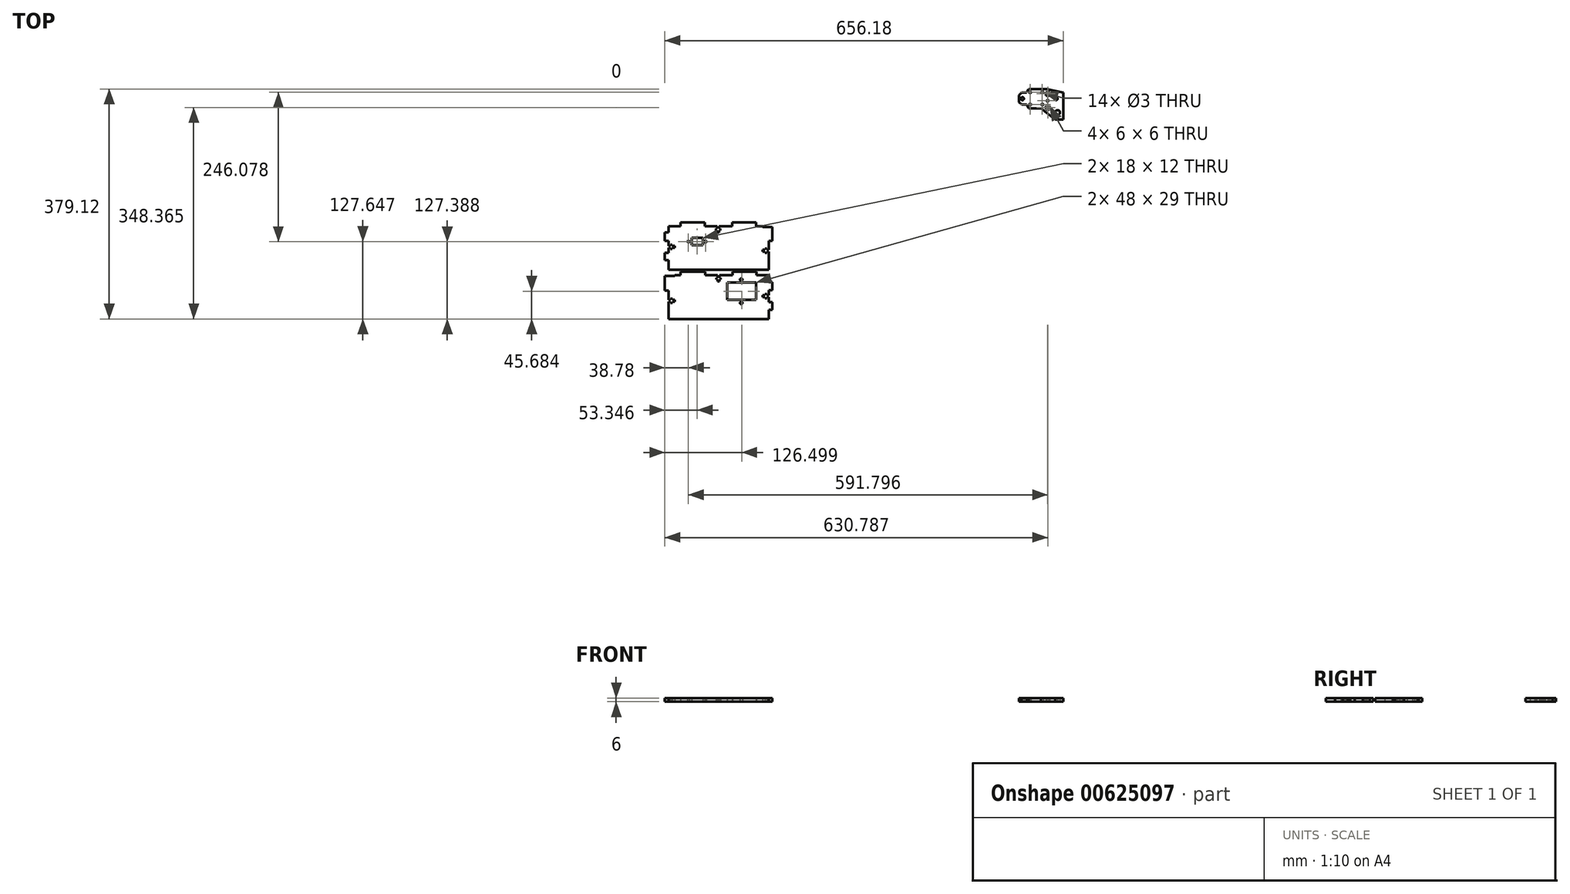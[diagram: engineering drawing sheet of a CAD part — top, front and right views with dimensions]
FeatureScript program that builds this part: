
annotation { "Feature Type Name" : "Feature", "Feature Type Description" : "" }
export const myFeature = defineFeature(function(context is Context, id is Id, definition is map)
    precondition{}
    {
        {
            var Q0;
            Q0=qCreatedBy(makeId("Top.planeOp"),FACE);
            var sketch = newSketch(context, id + "F0", { "sketchPlane" : qUnion([Q0])});
            skLineSegment(sketch, "E0", {"start": v(-400.96, 215.45) * mm, "end": v(-400.96, 196.55) * mm, "construction": true});
            skLineSegment(sketch, "E1", {"start": v(399.04, 218.3) * mm, "end": v(399.04, 197.18) * mm, "construction": true});
            skLineSegment(sketch, "E2", {"start": v(-18.25, 53.91) * mm, "end": v(81.75, 53.91) * mm});
            skLineSegment(sketch, "E3", {"start": v(81.75, 53.91) * mm, "end": v(81.75, 33.91) * mm});
            skLineSegment(sketch, "E4", {"start": v(81.75, 33.91) * mm, "end": v(41.75, -46.09) * mm});
            skLineSegment(sketch, "E5", {"start": v(41.75, -46.09) * mm, "end": v(21.75, -46.09) * mm});
            skLineSegment(sketch, "E6", {"start": v(21.75, -46.09) * mm, "end": v(-18.25, 33.91) * mm});
            skLineSegment(sketch, "E7", {"start": v(-18.25, 33.91) * mm, "end": v(-18.25, 53.91) * mm});
            skLineSegment(sketch, "E8", {"start": v(31.75, 53.91) * mm, "end": v(31.75, -82.9) * mm, "construction": true});
            skPoint(sketch, "E9", {"position": v(-362.77, -178.41) * mm});
            skPoint(sketch, "E10", {"position": v(-388.62, -185.6) * mm});
            skLineSegment(sketch, "E11.bottom", {"start": v(-388.62, -178.41) * mm, "end": v(-211.62, -178.41) * mm});
            skLineSegment(sketch, "E11.top", {"start": v(-388.62, -256.41) * mm, "end": v(-211.62, -256.41) * mm});
            skLineSegment(sketch, "E11.left", {"start": v(-388.62, -178.41) * mm, "end": v(-388.62, -256.41) * mm});
            skLineSegment(sketch, "E11.right", {"start": v(-211.62, -178.41) * mm, "end": v(-211.62, -256.41) * mm});
            skLineSegment(sketch, "E12", {"start": v(-388.62, -209.41) * mm, "end": v(-382.62, -209.41) * mm});
            skLineSegment(sketch, "E13", {"start": v(-382.62, -209.41) * mm, "end": v(-382.62, -256.41) * mm});
            skLineSegment(sketch, "E14", {"start": v(-322.26, -178.41) * mm, "end": v(-322.26, -184.41) * mm});
            skLineSegment(sketch, "E15", {"start": v(-322.26, -184.41) * mm, "end": v(-277.26, -184.41) * mm});
            skLineSegment(sketch, "E16", {"start": v(-277.26, -184.41) * mm, "end": v(-277.26, -178.41) * mm});
            skLineSegment(sketch, "E17", {"start": v(-388.62, -185.6) * mm, "end": v(-372.39, -185.6) * mm});
            skLineSegment(sketch, "E18", {"start": v(-372.39, -185.6) * mm, "end": v(-372.39, -184.41) * mm});
            skLineSegment(sketch, "E19", {"start": v(-372.39, -184.41) * mm, "end": v(-362.77, -184.41) * mm});
            skLineSegment(sketch, "E20", {"start": v(-362.77, -184.41) * mm, "end": v(-362.77, -178.41) * mm});
            skLineSegment(sketch, "E21", {"start": v(-237.45, -178.41) * mm, "end": v(-237.45, -184.41) * mm});
            skLineSegment(sketch, "E22", {"start": v(-237.45, -184.41) * mm, "end": v(-217.62, -184.41) * mm});
            skLineSegment(sketch, "E23", {"start": v(-217.62, -184.41) * mm, "end": v(-217.62, -195.47) * mm});
            skLineSegment(sketch, "E24", {"start": v(-217.62, -195.47) * mm, "end": v(-211.62, -195.47) * mm});
            skLineSegment(sketch, "E25", {"start": v(-211.62, -208.93) * mm, "end": v(-217.62, -208.93) * mm});
            skLineSegment(sketch, "E26", {"start": v(-217.62, -208.93) * mm, "end": v(-217.62, -228.93) * mm});
            skLineSegment(sketch, "E27", {"start": v(-217.62, -228.93) * mm, "end": v(-211.62, -228.93) * mm});
            skLineSegment(sketch, "E28", {"start": v(-211.62, -241.41) * mm, "end": v(-217.62, -241.41) * mm});
            skLineSegment(sketch, "E29", {"start": v(-217.62, -241.41) * mm, "end": v(-217.62, -256.41) * mm});
            skLineSegment(sketch, "E30.bottom", {"start": v(-286.12, -196.23) * mm, "end": v(-238.12, -196.23) * mm});
            skLineSegment(sketch, "E30.top", {"start": v(-286.12, -225.23) * mm, "end": v(-238.12, -225.23) * mm});
            skLineSegment(sketch, "E30.left", {"start": v(-286.12, -196.23) * mm, "end": v(-286.12, -225.23) * mm});
            skLineSegment(sketch, "E30.right", {"start": v(-238.12, -196.23) * mm, "end": v(-238.12, -225.23) * mm});
            skLineSegment(sketch, "E31", {"start": v(-382.62, -224.82) * mm, "end": v(-372.62, -224.82) * mm});
            skLineSegment(sketch, "E32", {"start": v(-372.62, -224.82) * mm, "end": v(-372.62, -227.82) * mm});
            skLineSegment(sketch, "E33", {"start": v(-372.62, -227.82) * mm, "end": v(-382.62, -227.82) * mm});
            skLineSegment(sketch, "E34", {"start": v(-379.34, -224.82) * mm, "end": v(-379.34, -222.82) * mm});
            skLineSegment(sketch, "E35", {"start": v(-379.34, -222.82) * mm, "end": v(-376.34, -222.82) * mm});
            skLineSegment(sketch, "E36", {"start": v(-376.34, -222.82) * mm, "end": v(-376.34, -224.82) * mm});
            skLineSegment(sketch, "E37", {"start": v(-379.27, -227.82) * mm, "end": v(-379.27, -229.82) * mm});
            skLineSegment(sketch, "E38", {"start": v(-379.27, -229.82) * mm, "end": v(-376.27, -229.82) * mm});
            skLineSegment(sketch, "E39", {"start": v(-376.27, -229.82) * mm, "end": v(-376.27, -227.82) * mm});
            skLineSegment(sketch, "E40", {"start": v(-301.63, -184.41) * mm, "end": v(-301.63, -194.41) * mm});
            skLineSegment(sketch, "E41", {"start": v(-301.63, -194.41) * mm, "end": v(-298.63, -194.41) * mm});
            skLineSegment(sketch, "E42", {"start": v(-298.63, -194.41) * mm, "end": v(-298.63, -184.41) * mm});
            skLineSegment(sketch, "E43", {"start": v(-303.63, -188.41) * mm, "end": v(-301.63, -188.41) * mm});
            skLineSegment(sketch, "E44", {"start": v(-296.63, -188.41) * mm, "end": v(-296.63, -191.41) * mm});
            skLineSegment(sketch, "E45", {"start": v(-296.63, -191.41) * mm, "end": v(-298.63, -191.41) * mm});
            skLineSegment(sketch, "E46.trimOffspring", {"start": v(-298.63, -188.41) * mm, "end": v(-296.63, -188.41) * mm});
            skLineSegment(sketch, "E47.trimOffspring", {"start": v(-301.63, -191.41) * mm, "end": v(-303.63, -191.41) * mm});
            skLineSegment(sketch, "E48", {"start": v(-303.63, -188.41) * mm, "end": v(-303.63, -191.41) * mm});
            skLineSegment(sketch, "E49", {"start": v(-217.62, -217.26) * mm, "end": v(-227.62, -217.26) * mm});
            skLineSegment(sketch, "E50", {"start": v(-227.62, -217.26) * mm, "end": v(-227.62, -220.26) * mm});
            skLineSegment(sketch, "E51", {"start": v(-227.62, -220.26) * mm, "end": v(-217.62, -220.26) * mm});
            skLineSegment(sketch, "E52.bottom", {"start": v(-223.46, -215.26) * mm, "end": v(-220.46, -215.26) * mm});
            skLineSegment(sketch, "E52.top", {"start": v(-223.46, -222.26) * mm, "end": v(-220.46, -222.26) * mm});
            skLineSegment(sketch, "E52.left", {"start": v(-223.46, -215.26) * mm, "end": v(-223.46, -222.26) * mm});
            skLineSegment(sketch, "E52.right", {"start": v(-220.46, -215.26) * mm, "end": v(-220.46, -222.26) * mm});
            skCircle(sketch, "E53", {"center": v(-262.81, -191.54) * mm, "radius": 2 * mm});
            skCircle(sketch, "E54", {"center": v(-262.81, -230.07) * mm, "radius": 2 * mm});
            skPoint(sketch, "E55", {"position": v(-362.84, -97.6) * mm});
            skLineSegment(sketch, "E56.bottom", {"start": v(-388.62, -97.6) * mm, "end": v(-211.62, -97.6) * mm});
            skLineSegment(sketch, "E56.top", {"start": v(-388.62, -175.6) * mm, "end": v(-211.62, -175.6) * mm});
            skLineSegment(sketch, "E56.left", {"start": v(-388.62, -97.6) * mm, "end": v(-388.62, -175.6) * mm});
            skLineSegment(sketch, "E56.right", {"start": v(-211.62, -97.6) * mm, "end": v(-211.62, -175.6) * mm});
            skLineSegment(sketch, "E57", {"start": v(-388.62, -113.85) * mm, "end": v(-382.62, -113.85) * mm});
            skLineSegment(sketch, "E58", {"start": v(-382.62, -113.85) * mm, "end": v(-382.62, -103.59) * mm});
            skLineSegment(sketch, "E59", {"start": v(-382.62, -103.59) * mm, "end": v(-362.62, -103.59) * mm});
            skLineSegment(sketch, "E60", {"start": v(-362.62, -103.59) * mm, "end": v(-362.84, -97.6) * mm});
            skLineSegment(sketch, "E61", {"start": v(-322.93, -97.6) * mm, "end": v(-322.93, -103.6) * mm});
            skLineSegment(sketch, "E62", {"start": v(-322.93, -103.6) * mm, "end": v(-277.93, -103.6) * mm});
            skLineSegment(sketch, "E63", {"start": v(-277.93, -103.6) * mm, "end": v(-277.93, -97.6) * mm});
            skLineSegment(sketch, "E64", {"start": v(-388.62, -127.72) * mm, "end": v(-382.62, -127.72) * mm});
            skLineSegment(sketch, "E65", {"start": v(-382.62, -127.72) * mm, "end": v(-382.62, -147.72) * mm});
            skLineSegment(sketch, "E66", {"start": v(-382.62, -147.72) * mm, "end": v(-390.27, -147.72) * mm});
            skLineSegment(sketch, "E67", {"start": v(-388.62, -159.6) * mm, "end": v(-382.62, -159.6) * mm});
            skLineSegment(sketch, "E68", {"start": v(-382.62, -159.6) * mm, "end": v(-382.62, -175.6) * mm});
            skLineSegment(sketch, "E69.bottom", {"start": v(-344.27, -122.76) * mm, "end": v(-326.27, -122.76) * mm});
            skLineSegment(sketch, "E69.top", {"start": v(-344.27, -134.76) * mm, "end": v(-326.27, -134.76) * mm});
            skLineSegment(sketch, "E69.left", {"start": v(-344.27, -122.76) * mm, "end": v(-344.27, -134.76) * mm});
            skLineSegment(sketch, "E69.right", {"start": v(-326.27, -122.76) * mm, "end": v(-326.27, -134.76) * mm});
            skCircle(sketch, "E70", {"center": v(-321.57, -129.02) * mm, "radius": 1.5 * mm});
            skCircle(sketch, "E71", {"center": v(-349.84, -129.02) * mm, "radius": 1.5 * mm});
            skLineSegment(sketch, "E72", {"start": v(-211.62, -127.6) * mm, "end": v(-217.62, -127.6) * mm});
            skLineSegment(sketch, "E73", {"start": v(-217.62, -127.6) * mm, "end": v(-217.62, -175.6) * mm});
            skLineSegment(sketch, "E74", {"start": v(-238.62, -97.6) * mm, "end": v(-238.62, -103.6) * mm});
            skLineSegment(sketch, "E75", {"start": v(-238.62, -103.6) * mm, "end": v(-227.62, -103.6) * mm});
            skLineSegment(sketch, "E76", {"start": v(-227.62, -103.6) * mm, "end": v(-227.62, -104.6) * mm});
            skLineSegment(sketch, "E77", {"start": v(-227.62, -104.6) * mm, "end": v(-211.62, -104.6) * mm});
            skLineSegment(sketch, "E78.bottom", {"start": v(-382.62, -135.99) * mm, "end": v(-372.62, -135.99) * mm});
            skLineSegment(sketch, "E78.top", {"start": v(-382.62, -138.99) * mm, "end": v(-372.62, -138.99) * mm});
            skLineSegment(sketch, "E78.left", {"start": v(-382.62, -135.99) * mm, "end": v(-382.62, -138.99) * mm});
            skLineSegment(sketch, "E78.right", {"start": v(-372.62, -135.99) * mm, "end": v(-372.62, -138.99) * mm});
            skLineSegment(sketch, "E79.bottom", {"start": v(-302.3, -103.6) * mm, "end": v(-299.3, -103.6) * mm});
            skLineSegment(sketch, "E79.top", {"start": v(-302.3, -113.6) * mm, "end": v(-299.3, -113.6) * mm});
            skLineSegment(sketch, "E79.left", {"start": v(-302.3, -103.6) * mm, "end": v(-302.3, -113.6) * mm});
            skLineSegment(sketch, "E79.right", {"start": v(-299.3, -103.6) * mm, "end": v(-299.3, -113.6) * mm});
            skLineSegment(sketch, "E80.bottom", {"start": v(-217.62, -142.67) * mm, "end": v(-227.62, -142.67) * mm});
            skLineSegment(sketch, "E80.top", {"start": v(-217.62, -145.67) * mm, "end": v(-227.62, -145.67) * mm});
            skLineSegment(sketch, "E80.left", {"start": v(-217.62, -142.67) * mm, "end": v(-217.62, -145.67) * mm});
            skLineSegment(sketch, "E80.right", {"start": v(-227.62, -142.67) * mm, "end": v(-227.62, -145.67) * mm});
            skLineSegment(sketch, "E81.bottom", {"start": v(-223.76, -140.67) * mm, "end": v(-220.76, -140.67) * mm});
            skLineSegment(sketch, "E81.top", {"start": v(-223.76, -147.67) * mm, "end": v(-220.76, -147.67) * mm});
            skLineSegment(sketch, "E81.left", {"start": v(-223.76, -140.67) * mm, "end": v(-223.76, -147.67) * mm});
            skLineSegment(sketch, "E81.right", {"start": v(-220.76, -140.67) * mm, "end": v(-220.76, -147.67) * mm});
            skLineSegment(sketch, "E82.bottom", {"start": v(-304.3, -107.4) * mm, "end": v(-297.3, -107.4) * mm});
            skLineSegment(sketch, "E82.top", {"start": v(-304.3, -110.4) * mm, "end": v(-297.3, -110.4) * mm});
            skLineSegment(sketch, "E82.left", {"start": v(-304.3, -107.4) * mm, "end": v(-304.3, -110.4) * mm});
            skLineSegment(sketch, "E82.right", {"start": v(-297.3, -107.4) * mm, "end": v(-297.3, -110.4) * mm});
            skLineSegment(sketch, "E83.bottom", {"start": v(-379.61, -133.99) * mm, "end": v(-376.61, -133.99) * mm});
            skLineSegment(sketch, "E83.top", {"start": v(-379.61, -140.99) * mm, "end": v(-376.61, -140.99) * mm});
            skLineSegment(sketch, "E83.left", {"start": v(-379.61, -133.99) * mm, "end": v(-379.61, -140.99) * mm});
            skLineSegment(sketch, "E83.right", {"start": v(-376.61, -133.99) * mm, "end": v(-376.61, -140.99) * mm});
            skLineSegment(sketch, "E84", {"start": v(210.6, 122.7) * mm, "end": v(240.6, 122.7) * mm});
            skLineSegment(sketch, "E85", {"start": v(240.6, 122.7) * mm, "end": v(267.56, 116.54) * mm});
            skLineSegment(sketch, "E86", {"start": v(267.56, 116.54) * mm, "end": v(267.56, 72.54) * mm});
            skLineSegment(sketch, "E87", {"start": v(267.56, 72.54) * mm, "end": v(254.56, 72.54) * mm});
            skLineSegment(sketch, "E88", {"start": v(254.56, 72.54) * mm, "end": v(230.6, 90.7) * mm});
            skLineSegment(sketch, "E89", {"start": v(230.6, 90.7) * mm, "end": v(210.6, 90.7) * mm});
            skLineSegment(sketch, "E90", {"start": v(210.6, 90.7) * mm, "end": v(207.37, 96.71) * mm});
            skLineSegment(sketch, "E91", {"start": v(207.37, 96.71) * mm, "end": v(199.07, 96.71) * mm});
            skLineSegment(sketch, "E92", {"start": v(199.07, 96.71) * mm, "end": v(194.7, 101.07) * mm});
            skLineSegment(sketch, "E93", {"start": v(194.7, 101.07) * mm, "end": v(194.7, 112.35) * mm});
            skLineSegment(sketch, "E94", {"start": v(194.7, 112.35) * mm, "end": v(199.07, 116.71) * mm});
            skLineSegment(sketch, "E95", {"start": v(199.07, 116.71) * mm, "end": v(207.37, 116.71) * mm});
            skLineSegment(sketch, "E96", {"start": v(207.37, 116.71) * mm, "end": v(210.6, 122.7) * mm});
            skLineSegment(sketch, "E97.bottom", {"start": v(239.2, 117.5) * mm, "end": v(245.2, 117.5) * mm});
            skLineSegment(sketch, "E97.top", {"start": v(239.2, 111.5) * mm, "end": v(245.2, 111.5) * mm});
            skLineSegment(sketch, "E97.left", {"start": v(239.2, 117.5) * mm, "end": v(239.2, 111.5) * mm});
            skLineSegment(sketch, "E97.right", {"start": v(245.2, 117.5) * mm, "end": v(245.2, 111.5) * mm});
            skLineSegment(sketch, "E98.bottom", {"start": v(239.17, 94.96) * mm, "end": v(245.17, 94.96) * mm});
            skLineSegment(sketch, "E98.top", {"start": v(239.17, 88.96) * mm, "end": v(245.17, 88.96) * mm});
            skLineSegment(sketch, "E98.left", {"start": v(239.17, 94.96) * mm, "end": v(239.17, 88.96) * mm});
            skLineSegment(sketch, "E98.right", {"start": v(245.17, 94.96) * mm, "end": v(245.17, 88.96) * mm});
            skCircle(sketch, "E99", {"center": v(200.33, 106.71) * mm, "radius": 2.5 * mm});
            skCircle(sketch, "E100", {"center": v(213.14, 117.06) * mm, "radius": 1.5 * mm});
            skCircle(sketch, "E101", {"center": v(213.14, 97.06) * mm, "radius": 1.5 * mm});
            skCircle(sketch, "E102", {"center": v(233.14, 97.06) * mm, "radius": 1.5 * mm});
            skCircle(sketch, "E103", {"center": v(233.14, 117.06) * mm, "radius": 1.5 * mm});
            skCircle(sketch, "E104", {"center": v(241.96, 103.18) * mm, "radius": 1.5 * mm});
            skCircle(sketch, "E105", {"center": v(255.73, 106.71) * mm, "radius": 2.5 * mm});
            skCircle(sketch, "E106", {"center": v(258.28, 83.74) * mm, "radius": 4 * mm});
            skLineSegment(sketch, "E107", {"start": v(192.03, 106.71) * mm, "end": v(273.18, 106.71) * mm, "construction": true});
            skSolve(sketch);
        }
        {
            var Q0;
            {var subQ25=sQuery(id+"F0.wireOp",EDGE,"E12");Q0=makeQuery(id+"F0.imprint","IMPRINT",FACE,{"disambiguationData":[TD([[makeQuery(id+"F0.imprint","IMPRINT",EDGE,{"derivedFrom":subQ25}),1.0]])]});}
            extrude(context, id + "F1", {"entities" : qUnion([Q0]), "depth" : 6 * mm, "offsetDistance" : 25 * mm});
        }
        {
            var Q0;
            {var subQ31=sQuery(id+"F0.wireOp",EDGE,"E57");Q0=makeQuery(id+"F0.imprint","IMPRINT",FACE,{"disambiguationData":[TD([[makeQuery(id+"F0.imprint","IMPRINT",EDGE,{"derivedFrom":subQ31}),-1.0]])]});}
            extrude(context, id + "F2", {"entities" : qUnion([Q0]), "depth" : 6 * mm, "offsetDistance" : 25 * mm});
        }
        {
            var Q0;
            Q0=makeQuery(id+"F0.imprint","IMPRINT",FACE,{"disambiguationData":[TD([[makeQuery(id+"F0.imprint","IMPRINT",EDGE,{"derivedFrom":sQuery(id+"F0.wireOp",EDGE,"E84")}),-1.0]])]});
            extrude(context, id + "F3", {"entities" : qUnion([Q0]), "depth" : 6 * mm, "offsetDistance" : 25 * mm});
        }
        {
            var Q0;
            Q0=sQuery(id+"F0.wireOp",VERTEX,"E100.center");
            var Q1;
            Q1=sQuery(id+"F0.wireOp",VERTEX,"E103.center");
            var Q2;
            Q2=sQuery(id+"F0.wireOp",VERTEX,"E101.center");
            var Q3;
            Q3=sQuery(id+"F0.wireOp",VERTEX,"E102.center");
            var Q4;
            Q4=sQuery(id+"F0.wireOp",VERTEX,"E104.center");
            var Q5;
            Q5=makeQuery(id+"F3.opExtrude","SWEPT_BODY",BODY,{"disambiguationData":[OSD([sQuery(id+"F0.wireOp",EDGE,"E84"),sQuery(id+"F0.wireOp",EDGE,"E85"),sQuery(id+"F0.wireOp",EDGE,"E86"),sQuery(id+"F0.wireOp",EDGE,"E87"),sQuery(id+"F0.wireOp",EDGE,"E88"),sQuery(id+"F0.wireOp",EDGE,"E89"),sQuery(id+"F0.wireOp",EDGE,"E90"),sQuery(id+"F0.wireOp",EDGE,"E91"),sQuery(id+"F0.wireOp",EDGE,"E92"),sQuery(id+"F0.wireOp",EDGE,"E93"),sQuery(id+"F0.wireOp",EDGE,"E94"),sQuery(id+"F0.wireOp",EDGE,"E95"),sQuery(id+"F0.wireOp",EDGE,"E96"),sQuery(id+"F0.wireOp",EDGE,"E97.bottom"),sQuery(id+"F0.wireOp",EDGE,"E97.top"),sQuery(id+"F0.wireOp",EDGE,"E97.left"),sQuery(id+"F0.wireOp",EDGE,"E97.right"),sQuery(id+"F0.wireOp",EDGE,"E98.bottom"),sQuery(id+"F0.wireOp",EDGE,"E98.top"),sQuery(id+"F0.wireOp",EDGE,"E98.left"),sQuery(id+"F0.wireOp",EDGE,"E98.right"),sQuery(id+"F0.wireOp",EDGE,"E99"),sQuery(id+"F0.wireOp",EDGE,"E100"),sQuery(id+"F0.wireOp",EDGE,"E101"),sQuery(id+"F0.wireOp",EDGE,"E102"),sQuery(id+"F0.wireOp",EDGE,"E103"),sQuery(id+"F0.wireOp",EDGE,"E104"),sQuery(id+"F0.wireOp",EDGE,"E105"),sQuery(id+"F0.wireOp",EDGE,"E106")])]});
            hole(context, id + "F4", {"style" : HoleStyle.C_BORE, "endStyle" : HoleEndStyle.THROUGH, "standardTappedOrClearance" : lookupTablePath({ "standard" : "ISO", "size" : "3", "type" : "Drilled" }), "standardBlindInLast" : lookupTablePath({ "standard" : "ISO", "size" : "3", "type" : "Drilled" }), "holeDiameter" : 3 * mm, "cBoreDiameter" : 6 * mm, "cBoreDepth" : 2 * mm, "majorDiameter" : 5 * mm, "tappedDepth" : 12 * mm, "tapClearance" : 3, "locations" : qUnion([Q0, Q1, Q2, Q3, Q4]), "scope" : qUnion([Q5])});
        }
    });
